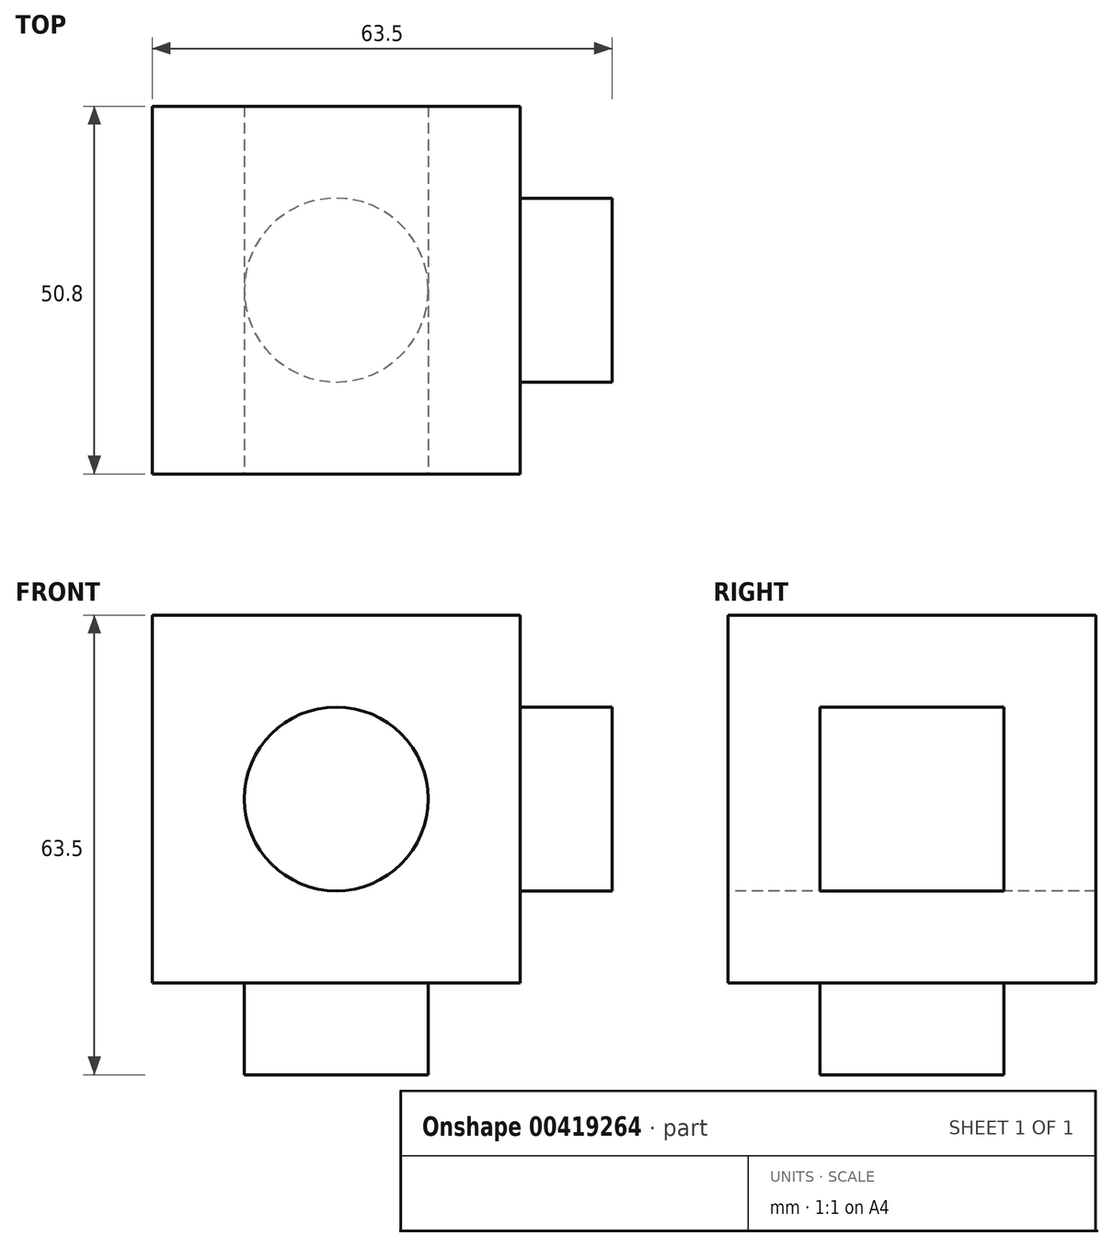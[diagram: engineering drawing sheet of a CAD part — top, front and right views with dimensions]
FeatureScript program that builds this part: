
annotation { "Feature Type Name" : "Feature", "Feature Type Description" : "" }
export const myFeature = defineFeature(function(context is Context, id is Id, definition is map)
    precondition{}
    {
        {
            var Q0;
            Q0=qCreatedBy(makeId("Front.planeOp"),FACE);
            var sketch = newSketch(context, id + "F0", { "sketchPlane" : qUnion([Q0])});
            skLineSegment(sketch, "E0.bottom", {"start": v(0, 0) * mm, "end": v(-50.8, 0) * mm});
            skLineSegment(sketch, "E0.top", {"start": v(0, 50.8) * mm, "end": v(-50.8, 50.8) * mm});
            skLineSegment(sketch, "E0.left", {"start": v(0, 0) * mm, "end": v(0, 50.8) * mm});
            skLineSegment(sketch, "E0.right", {"start": v(-50.8, 0) * mm, "end": v(-50.8, 50.8) * mm});
            skSolve(sketch);
        }
        {
            var Q0;
            Q0 = qSketchRegion(id + "F0", true);
            extrude(context, id + "F1", {"entities" : qUnion([Q0]), "depth" : 50.8 * mm});
        }
        {
            var Q0;
            Q0=makeQuery(id+"F1.opExtrude","CAP_FACE",FACE,{"disambiguationData":[OSD([sQuery(id+"F0.wireOp",EDGE,"E0.bottom"),sQuery(id+"F0.wireOp",EDGE,"E0.top"),sQuery(id+"F0.wireOp",EDGE,"E0.left"),sQuery(id+"F0.wireOp",EDGE,"E0.right")])],"isStart":false});
            var sketch = newSketch(context, id + "F2", { "sketchPlane" : qUnion([Q0])});
            skCircle(sketch, "E1", {"center": v(-25.4, 25.4) * mm, "radius": 12.7 * mm});
            skSolve(sketch);
        }
        {
            var Q0;
            Q0 = qSketchRegion(id + "F2", true);
            extrude(context, id + "F3", {"entities" : qUnion([Q0]), "operationType" : NewBodyOperationType.REMOVE, "oppositeDirection" : true, "depth" : 50.8 * mm});
        }
        {
            var Q0;
            Q0=makeQuery(id+"F1.opExtrude","SWEPT_FACE",FACE,{"disambiguationData":[OSD([sQuery(id+"F0.wireOp",EDGE,"E0.left")])]});
            var sketch = newSketch(context, id + "F4", { "sketchPlane" : qUnion([Q0])});
            skLineSegment(sketch, "E2.bottom", {"start": v(-38.1, 38.1) * mm, "end": v(-12.7, 38.1) * mm});
            skLineSegment(sketch, "E2.top", {"start": v(-38.1, 12.7) * mm, "end": v(-12.7, 12.7) * mm});
            skLineSegment(sketch, "E2.left", {"start": v(-38.1, 38.1) * mm, "end": v(-38.1, 12.7) * mm});
            skLineSegment(sketch, "E2.right", {"start": v(-12.7, 38.1) * mm, "end": v(-12.7, 12.7) * mm});
            skSolve(sketch);
        }
        {
            var Q0;
            Q0 = qSketchRegion(id + "F4", true);
            extrude(context, id + "F5", {"entities" : qUnion([Q0]), "operationType" : NewBodyOperationType.ADD, "depth" : 12.7 * mm});
        }
        {
            var Q0;
            Q0=makeQuery(id+"F1.opExtrude","SWEPT_FACE",FACE,{"disambiguationData":[OSD([sQuery(id+"F0.wireOp",EDGE,"E0.bottom")])]});
            var sketch = newSketch(context, id + "F6", { "sketchPlane" : qUnion([Q0])});
            skCircle(sketch, "E3", {"center": v(-25.4, 25.4) * mm, "radius": 12.7 * mm});
            skSolve(sketch);
        }
        {
            var Q0;
            Q0 = qSketchRegion(id + "F6", true);
            extrude(context, id + "F7", {"entities" : qUnion([Q0]), "operationType" : NewBodyOperationType.ADD, "depth" : 12.7 * mm});
        }
    });
